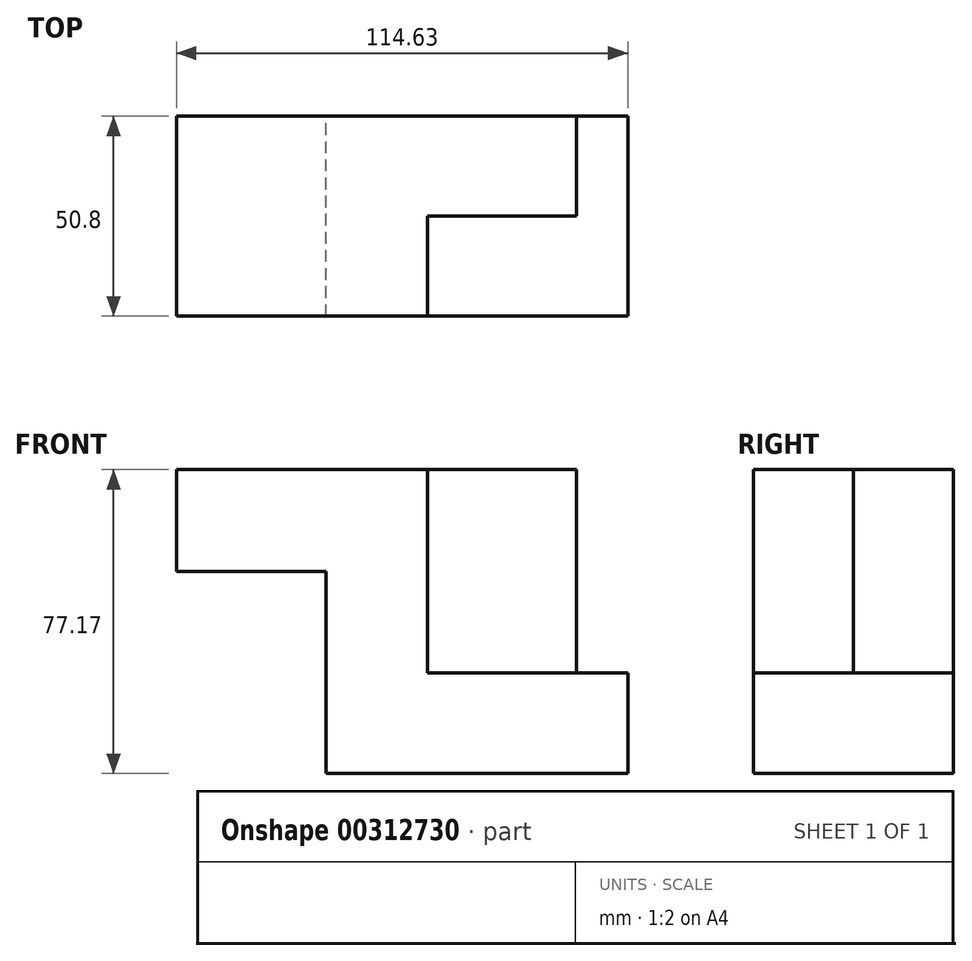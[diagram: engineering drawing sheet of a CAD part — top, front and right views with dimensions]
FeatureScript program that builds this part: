
annotation { "Feature Type Name" : "Feature", "Feature Type Description" : "" }
export const myFeature = defineFeature(function(context is Context, id is Id, definition is map)
    precondition{}
    {
        {
            var Q0;
            Q0=qCreatedBy(makeId("Front.planeOp"),FACE);
            var sketch = newSketch(context, id + "F0", { "sketchPlane" : qUnion([Q0])});
            skLineSegment(sketch, "E0", {"start": v(-63.7, 48.23) * mm, "end": v(-63.7, 22.41) * mm});
            skLineSegment(sketch, "E1", {"start": v(-63.7, 22.41) * mm, "end": v(-25.68, 22.41) * mm});
            skLineSegment(sketch, "E2", {"start": v(-25.68, 22.41) * mm, "end": v(-25.68, -28.94) * mm});
            skLineSegment(sketch, "E3", {"start": v(-25.68, -28.94) * mm, "end": v(50.93, -28.94) * mm});
            skLineSegment(sketch, "E4", {"start": v(50.93, -28.94) * mm, "end": v(50.93, -3.4) * mm});
            skLineSegment(sketch, "E5", {"start": v(50.93, -3.4) * mm, "end": v(0, -3.4) * mm});
            skLineSegment(sketch, "E6", {"start": v(0, -3.4) * mm, "end": v(0, 48.23) * mm});
            skLineSegment(sketch, "E7", {"start": v(0, 48.23) * mm, "end": v(-63.7, 48.23) * mm});
            skLineSegment(sketch, "E8", {"start": v(50.93, -3.4) * mm, "end": v(37.88, -3.4) * mm});
            skLineSegment(sketch, "E9", {"start": v(37.88, 48.23) * mm, "end": v(37.88, -3.4) * mm});
            skLineSegment(sketch, "E10", {"start": v(37.88, 48.23) * mm, "end": v(0, 48.23) * mm});
            skSolve(sketch);
        }
        {
            var Q0;
            Q0=makeQuery(id+"F0.imprint","IMPRINT",FACE,{"disambiguationData":[TD([[makeQuery(id+"F0.imprint","IMPRINT",EDGE,{"derivedFrom":sQuery(id+"F0.wireOp",EDGE,"E0")}),1.0]])]});
            extrude(context, id + "F1", {"entities" : qUnion([Q0]), "depth" : 50.8 * mm});
        }
        {
            var Q0;
            Q0=makeQuery(id+"F0.imprint","IMPRINT",FACE,{"disambiguationData":[TD([[makeQuery(id+"F0.imprint","IMPRINT",EDGE,{"derivedFrom":sQuery(id+"F0.wireOp",EDGE,"E5")}),-1.0]])]});
            extrude(context, id + "F2", {"entities" : qUnion([Q0]), "operationType" : NewBodyOperationType.ADD, "depth" : 25.4 * mm});
        }
    });
